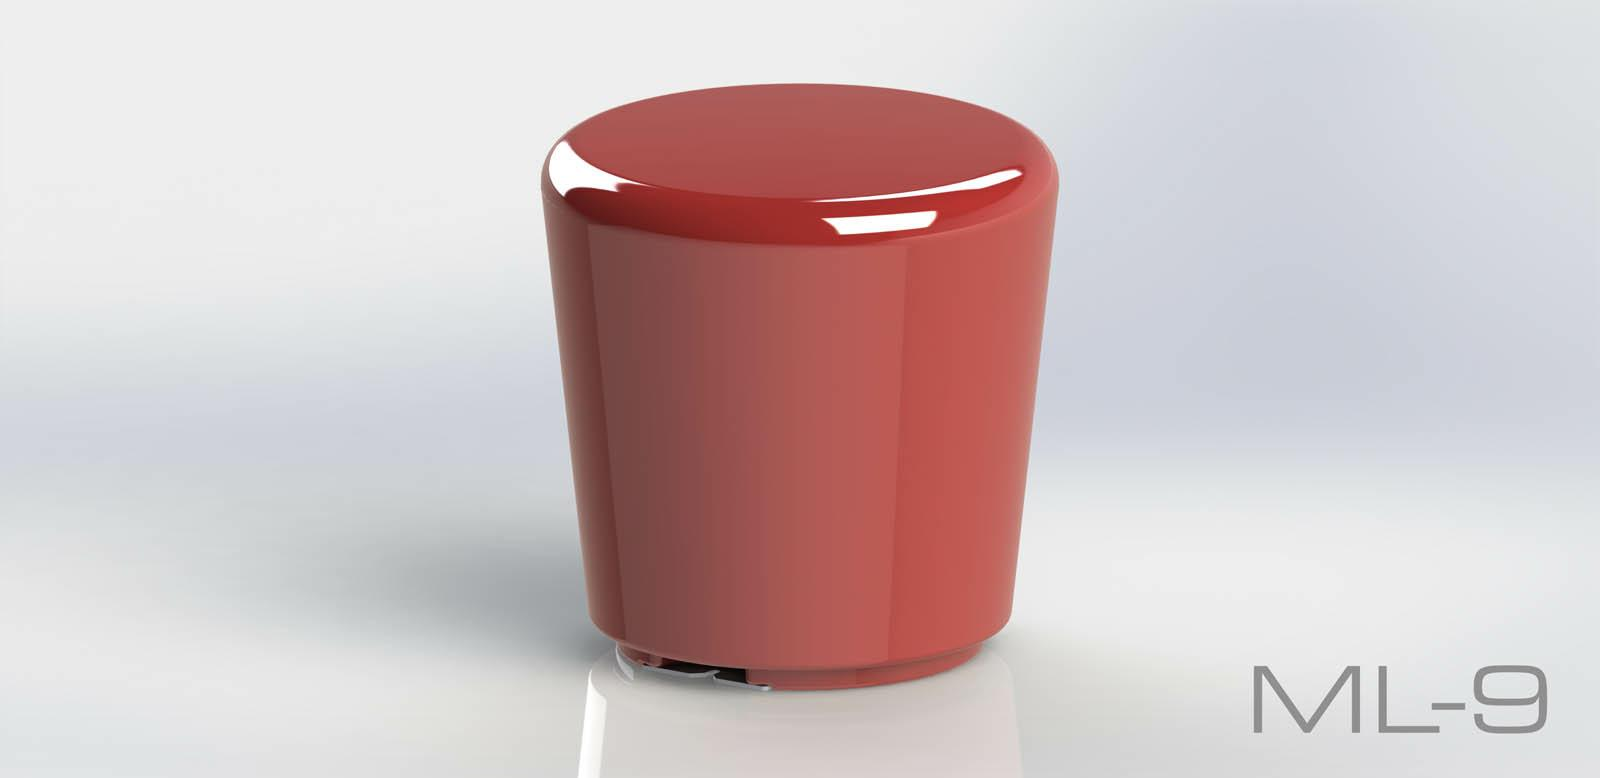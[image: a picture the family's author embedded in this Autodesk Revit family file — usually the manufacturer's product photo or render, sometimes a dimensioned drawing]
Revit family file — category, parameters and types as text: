
# Revit family: Modullaro ML 09
name_source: partatom
category: Meble
revit_build: Autodesk Revit 2018 (Build: 20190510_1515(x64)
units: mm (PartAtom-declared; Revit-internal decimal feet)

## family parameters
Numer OmniClass = 23.40.10.11.14
Obiekt nadrzędny = Powierzchnia
Punkt obliczania pomieszczeń = Nie
Tnij formami wycięć po wczytaniu = Nie
Tytuł OmniClass = Exterior Seating
Współdzielony = Nie

## types (1)
- Modullaro ML 09
    Domyślna rzędna = 1219 mm
    Długość = 491 mm  [stored 1.61089 ft]
    IfcExportAs = IfcFurnishingElement
    Komentarze do typu = Ławka
    Materiał - informacja = Szeroki wybór kolorów wg palety RAL. Istnieje również możliwość specjalnego wykonania kolorystycznego na indywidualne zapytanie klienta.
    Model = Modullaro ML 09
    Obraz typu = ML-9.jpg
    Producent = Astrini Design
    Szerokość = 491 mm  [stored 1.61089 ft]
    Temepratura użytkowania = -40°C do 80°C, ( -40°F do 176°F )
    URL = http://astrini-design.pl
    Waga (szacunkowo) = 7.00 kg
    Wysokość = 500 mm  [stored 1.64042 ft]

note: [stored X ft] marks values corroborated as IEEE doubles in the binary element streams (Revit-internal decimal feet)
